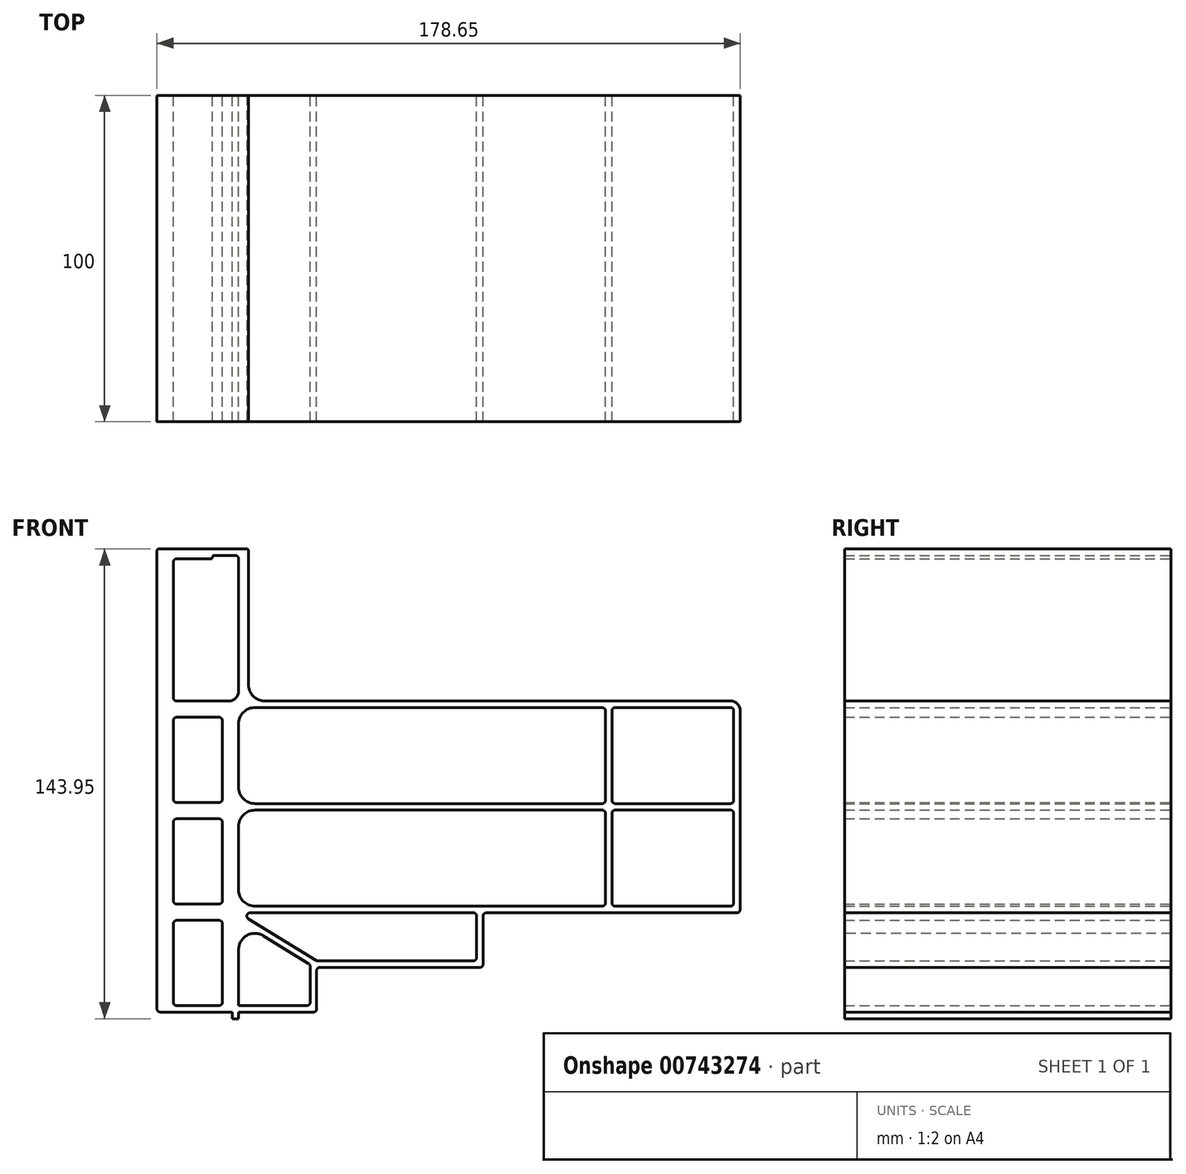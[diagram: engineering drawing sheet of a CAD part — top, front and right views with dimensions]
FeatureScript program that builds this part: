
annotation { "Feature Type Name" : "Feature", "Feature Type Description" : "" }
export const myFeature = defineFeature(function(context is Context, id is Id, definition is map)
    precondition{}
    {
        {
            var Q0;
            Q0=qCreatedBy(makeId("Front.planeOp"),FACE);
            var sketch = newSketch(context, id + "F0", { "sketchPlane" : qUnion([Q0])});
            skLineSegment(sketch, "E0", {"start": v(0, 0) * mm, "end": v(23, 0) * mm});
            skLineSegment(sketch, "E1", {"start": v(23, 0) * mm, "end": v(23, -2) * mm});
            skLineSegment(sketch, "E2", {"start": v(23, -2) * mm, "end": v(25, -2) * mm});
            skLineSegment(sketch, "E3", {"start": v(25, -2) * mm, "end": v(25, 0) * mm});
            skLineSegment(sketch, "E4", {"start": v(25, 0) * mm, "end": v(48.9, 0) * mm});
            skLineSegment(sketch, "E5", {"start": v(48.9, 0) * mm, "end": v(48.9, 13.72) * mm});
            skLineSegment(sketch, "E6", {"start": v(48.9, 15.72) * mm, "end": v(25, 30.47) * mm});
            skLineSegment(sketch, "E7", {"start": v(25, 30.47) * mm, "end": v(97.9, 30.47) * mm});
            skLineSegment(sketch, "E8", {"start": v(178.65, 30.47) * mm, "end": v(178.65, 95.36) * mm});
            skLineSegment(sketch, "E9", {"start": v(178.65, 95.36) * mm, "end": v(28, 95.36) * mm});
            skLineSegment(sketch, "E10", {"start": v(28, 141.95) * mm, "end": v(0, 141.95) * mm});
            skLineSegment(sketch, "E11", {"start": v(0, 141.95) * mm, "end": v(0, 0) * mm});
            skLineSegment(sketch, "E12", {"start": v(20, 90.36) * mm, "end": v(20, 64.24) * mm});
            skLineSegment(sketch, "E13", {"start": v(5, 33.12) * mm, "end": v(20, 33.12) * mm});
            skLineSegment(sketch, "E14", {"start": v(5, 33.12) * mm, "end": v(5, 59.24) * mm});
            skLineSegment(sketch, "E15", {"start": v(5, 59.24) * mm, "end": v(20, 59.24) * mm});
            skLineSegment(sketch, "E16", {"start": v(5, 64.24) * mm, "end": v(20, 64.24) * mm});
            skLineSegment(sketch, "E17.trimOffspring", {"start": v(5, 64.24) * mm, "end": v(5, 90.36) * mm});
            skLineSegment(sketch, "E18.trimOffspring", {"start": v(20, 59.24) * mm, "end": v(20, 33.12) * mm});
            skLineSegment(sketch, "E19", {"start": v(20, 28.12) * mm, "end": v(20, 2) * mm});
            skLineSegment(sketch, "E20", {"start": v(5, 2) * mm, "end": v(20, 2) * mm});
            skLineSegment(sketch, "E21", {"start": v(5, 2) * mm, "end": v(5, 28.12) * mm});
            skLineSegment(sketch, "E22", {"start": v(20, 28.12) * mm, "end": v(5, 28.12) * mm});
            skLineSegment(sketch, "E23", {"start": v(25, 28.12) * mm, "end": v(46.9, 14.6) * mm});
            skLineSegment(sketch, "E24", {"start": v(46.9, 14.6) * mm, "end": v(46.9, 2) * mm});
            skLineSegment(sketch, "E25", {"start": v(46.9, 2) * mm, "end": v(25, 2) * mm});
            skLineSegment(sketch, "E26", {"start": v(25, 2) * mm, "end": v(25, 28.12) * mm});
            skLineSegment(sketch, "E27", {"start": v(25, 32.47) * mm, "end": v(137.35, 32.47) * mm});
            skLineSegment(sketch, "E28", {"start": v(137.35, 32.47) * mm, "end": v(137.35, 61.92) * mm});
            skLineSegment(sketch, "E29", {"start": v(137.35, 61.92) * mm, "end": v(25, 61.92) * mm});
            skLineSegment(sketch, "E30", {"start": v(25, 61.92) * mm, "end": v(25, 32.47) * mm});
            skLineSegment(sketch, "E31", {"start": v(25, 93.36) * mm, "end": v(25, 63.92) * mm});
            skLineSegment(sketch, "E32", {"start": v(25, 63.92) * mm, "end": v(137.35, 63.92) * mm});
            skLineSegment(sketch, "E33", {"start": v(137.35, 63.92) * mm, "end": v(137.35, 93.36) * mm});
            skLineSegment(sketch, "E34", {"start": v(25, 93.36) * mm, "end": v(137.35, 93.36) * mm});
            skLineSegment(sketch, "E35", {"start": v(139.35, 93.36) * mm, "end": v(176.65, 93.36) * mm});
            skLineSegment(sketch, "E36", {"start": v(176.65, 93.36) * mm, "end": v(176.65, 63.92) * mm});
            skLineSegment(sketch, "E37", {"start": v(176.65, 63.92) * mm, "end": v(139.35, 63.92) * mm});
            skLineSegment(sketch, "E38", {"start": v(139.35, 63.92) * mm, "end": v(139.35, 93.36) * mm});
            skLineSegment(sketch, "E39", {"start": v(139.35, 61.92) * mm, "end": v(139.35, 32.47) * mm});
            skLineSegment(sketch, "E40", {"start": v(139.35, 32.47) * mm, "end": v(176.65, 32.47) * mm});
            skLineSegment(sketch, "E41", {"start": v(176.65, 32.47) * mm, "end": v(176.65, 61.92) * mm});
            skLineSegment(sketch, "E42", {"start": v(176.65, 61.92) * mm, "end": v(139.35, 61.92) * mm});
            skLineSegment(sketch, "E43", {"start": v(5, 33.12) * mm, "end": v(5, 28.12) * mm, "construction": true});
            skLineSegment(sketch, "E44", {"start": v(5, 64.24) * mm, "end": v(5, 59.24) * mm, "construction": true});
            skLineSegment(sketch, "E45", {"start": v(137.35, 93.36) * mm, "end": v(139.35, 93.36) * mm, "construction": true});
            skLineSegment(sketch, "E46", {"start": v(25, 63.92) * mm, "end": v(25, 61.92) * mm, "construction": true});
            skLineSegment(sketch, "E47", {"start": v(25, 32.47) * mm, "end": v(25, 30.47) * mm, "construction": true});
            skLineSegment(sketch, "E48", {"start": v(25, 28.12) * mm, "end": v(25, 30.47) * mm, "construction": true});
            skLineSegment(sketch, "E49", {"start": v(25, 2) * mm, "end": v(5, 2) * mm, "construction": true});
            skLineSegment(sketch, "E50", {"start": v(137.35, 32.47) * mm, "end": v(139.35, 32.47) * mm, "construction": true});
            skLineSegment(sketch, "E51", {"start": v(176.65, 61.92) * mm, "end": v(176.65, 63.92) * mm, "construction": true});
            skLineSegment(sketch, "E52", {"start": v(137.35, 63.92) * mm, "end": v(137.35, 61.92) * mm, "construction": true});
            skLineSegment(sketch, "E53", {"start": v(31.21, 24.29) * mm, "end": v(32.26, 25.99) * mm, "construction": true});
            skLineSegment(sketch, "E54", {"start": v(46.9, 8.3) * mm, "end": v(48.9, 8.3) * mm, "construction": true});
            skLineSegment(sketch, "E55", {"start": v(24.57, 2) * mm, "end": v(24.57, 0) * mm, "construction": true});
            skLineSegment(sketch, "E56", {"start": v(48.9, 15.72) * mm, "end": v(97.9, 15.72) * mm});
            skLineSegment(sketch, "E57", {"start": v(97.9, 15.72) * mm, "end": v(97.9, 30.47) * mm});
            skLineSegment(sketch, "E58", {"start": v(99.9, 30.47) * mm, "end": v(99.9, 13.72) * mm});
            skLineSegment(sketch, "E59", {"start": v(99.9, 13.72) * mm, "end": v(48.9, 13.72) * mm});
            skLineSegment(sketch, "E60.trimOffspring", {"start": v(99.9, 30.47) * mm, "end": v(178.65, 30.47) * mm});
            skLineSegment(sketch, "E61", {"start": v(139.35, 63.92) * mm, "end": v(137.35, 63.92) * mm, "construction": true});
            skLineSegment(sketch, "E62", {"start": v(137.35, 61.92) * mm, "end": v(139.35, 61.92) * mm, "construction": true});
            skLineSegment(sketch, "E63", {"start": v(97.9, 30.47) * mm, "end": v(99.9, 30.47) * mm, "construction": true});
            skLineSegment(sketch, "E64", {"start": v(5, 95.36) * mm, "end": v(5, 138.95) * mm});
            skLineSegment(sketch, "E65", {"start": v(5, 90.36) * mm, "end": v(20, 90.36) * mm});
            skLineSegment(sketch, "E66", {"start": v(74.4, 13.72) * mm, "end": v(74.4, 15.72) * mm, "construction": true});
            skLineSegment(sketch, "E67", {"start": v(25, 2) * mm, "end": v(25, 0) * mm, "construction": true});
            skLineSegment(sketch, "E68", {"start": v(25, 18) * mm, "end": v(20, 18) * mm, "construction": true});
            skLineSegment(sketch, "E69", {"start": v(5, 2) * mm, "end": v(0, 2) * mm, "construction": true});
            skLineSegment(sketch, "E70", {"start": v(176.65, 32.47) * mm, "end": v(176.65, 30.47) * mm, "construction": true});
            skLineSegment(sketch, "E71", {"start": v(176.65, 32.47) * mm, "end": v(178.65, 32.47) * mm, "construction": true});
            skLineSegment(sketch, "E72", {"start": v(5, 95.36) * mm, "end": v(25, 95.36) * mm});
            skLineSegment(sketch, "E73", {"start": v(28, 141.95) * mm, "end": v(28, 95.36) * mm});
            skLineSegment(sketch, "E74", {"start": v(25, 139.95) * mm, "end": v(25, 95.36) * mm});
            skLineSegment(sketch, "E75", {"start": v(5, 138.95) * mm, "end": v(17, 138.95) * mm});
            skLineSegment(sketch, "E76", {"start": v(17, 138.95) * mm, "end": v(17, 139.95) * mm});
            skLineSegment(sketch, "E77", {"start": v(17, 139.95) * mm, "end": v(25, 139.95) * mm});
            skSolve(sketch);
        }
        {
            var Q0;
            Q0=makeQuery(id+"F0.imprint","IMPRINT",FACE,{"disambiguationData":[TD([[makeQuery(id+"F0.imprint","IMPRINT",EDGE,{"derivedFrom":sQuery(id+"F0.wireOp",EDGE,"E0")}),1.0]])]});
            extrude(context, id + "F1", {"entities" : qUnion([Q0]), "depth" : 100 * mm, "offsetDistance" : 25 * mm});
        }
        {
            var Q0;
            Q0=makeQuery(id+"F1.opExtrude","SWEPT_EDGE",EDGE,{"disambiguationData":[OSD([sQuery(id+"F0.wireOp",EDGE,"E9"),sQuery(id+"F0.wireOp",EDGE,"E73")])]});
            var Q1;
            Q1=makeQuery(id+"F1.opExtrude","SWEPT_EDGE",EDGE,{"disambiguationData":[OSD([sQuery(id+"F0.wireOp",EDGE,"E23"),sQuery(id+"F0.wireOp",EDGE,"E26")])]});
            var Q2;
            Q2=makeQuery(id+"F1.opExtrude","SWEPT_EDGE",EDGE,{"disambiguationData":[OSD([sQuery(id+"F0.wireOp",EDGE,"E27"),sQuery(id+"F0.wireOp",EDGE,"E30")])]});
            var Q3;
            Q3=makeQuery(id+"F1.opExtrude","SWEPT_EDGE",EDGE,{"disambiguationData":[OSD([sQuery(id+"F0.wireOp",EDGE,"E29"),sQuery(id+"F0.wireOp",EDGE,"E30")])]});
            var Q4;
            Q4=makeQuery(id+"F1.opExtrude","SWEPT_EDGE",EDGE,{"disambiguationData":[OSD([sQuery(id+"F0.wireOp",EDGE,"E31"),sQuery(id+"F0.wireOp",EDGE,"E34")])]});
            var Q5;
            Q5=makeQuery(id+"F1.opExtrude","SWEPT_EDGE",EDGE,{"disambiguationData":[OSD([sQuery(id+"F0.wireOp",EDGE,"E31"),sQuery(id+"F0.wireOp",EDGE,"E32")])]});
            fillet(context, id + "F2", {"entities" : qUnion([Q0, Q1, Q2, Q3, Q4, Q5]), "radius" : 5 * mm, "tangentPropagation" : true, "allowEdgeOverflow" : false});
        }
        {
            var Q0;
            Q0=makeQuery(id+"F1.opExtrude","SWEPT_EDGE",EDGE,{"disambiguationData":[OSD([sQuery(id+"F0.wireOp",EDGE,"696LTCtU-8L7l-0TQZ-7p5k-baEngQwWw874"),sQuery(id+"F0.wireOp",EDGE,"E64")])]});
            var Q1;
            Q1=makeQuery(id+"F1.opExtrude","SWEPT_EDGE",EDGE,{"disambiguationData":[OSD([sQuery(id+"F0.wireOp",EDGE,"E16"),sQuery(id+"F0.wireOp",EDGE,"E17.trimOffspring")])]});
            var Q2;
            Q2=makeQuery(id+"F1.opExtrude","SWEPT_EDGE",EDGE,{"disambiguationData":[OSD([sQuery(id+"F0.wireOp",EDGE,"E13"),sQuery(id+"F0.wireOp",EDGE,"E14")])]});
            var Q3;
            Q3=makeQuery(id+"F1.opExtrude","SWEPT_EDGE",EDGE,{"disambiguationData":[OSD([sQuery(id+"F0.wireOp",EDGE,"E20"),sQuery(id+"F0.wireOp",EDGE,"E21")])]});
            var Q4;
            Q4=makeQuery(id+"F1.opExtrude","SWEPT_EDGE",EDGE,{"disambiguationData":[OSD([sQuery(id+"F0.wireOp",EDGE,"E64"),sQuery(id+"F0.wireOp",EDGE,"BG8pf7Ll-KLwd-1KIG-Txls-kzz8Mmku1XrW")])]});
            var Q5;
            Q5=makeQuery(id+"F1.opExtrude","SWEPT_EDGE",EDGE,{"disambiguationData":[OSD([sQuery(id+"F0.wireOp",EDGE,"E17.trimOffspring"),sQuery(id+"F0.wireOp",EDGE,"E65")])]});
            var Q6;
            Q6=makeQuery(id+"F1.opExtrude","SWEPT_EDGE",EDGE,{"disambiguationData":[OSD([sQuery(id+"F0.wireOp",EDGE,"E14"),sQuery(id+"F0.wireOp",EDGE,"E15")])]});
            var Q7;
            Q7=makeQuery(id+"F1.opExtrude","SWEPT_EDGE",EDGE,{"disambiguationData":[OSD([sQuery(id+"F0.wireOp",EDGE,"E21"),sQuery(id+"F0.wireOp",EDGE,"E22")])]});
            var Q8;
            Q8=makeQuery(id+"F1.opExtrude","SWEPT_EDGE",EDGE,{"disambiguationData":[OSD([sQuery(id+"F0.wireOp",EDGE,"E19"),sQuery(id+"F0.wireOp",EDGE,"E22")])]});
            var Q9;
            Q9=makeQuery(id+"F1.opExtrude","SWEPT_EDGE",EDGE,{"disambiguationData":[OSD([sQuery(id+"F0.wireOp",EDGE,"E15"),sQuery(id+"F0.wireOp",EDGE,"E18.trimOffspring")])]});
            var Q10;
            Q10=makeQuery(id+"F1.opExtrude","SWEPT_EDGE",EDGE,{"disambiguationData":[OSD([sQuery(id+"F0.wireOp",EDGE,"E12"),sQuery(id+"F0.wireOp",EDGE,"E65")])]});
            var Q11;
            Q11=makeQuery(id+"F1.opExtrude","SWEPT_EDGE",EDGE,{"disambiguationData":[OSD([sQuery(id+"F0.wireOp",EDGE,"JW9Dk7mF-qHn0-8jiC-juDo-dlRvJ3E6QT4r"),sQuery(id+"F0.wireOp",EDGE,"BG8pf7Ll-KLwd-1KIG-Txls-kzz8Mmku1XrW")])]});
            var Q12;
            Q12=makeQuery(id+"F1.opExtrude","SWEPT_EDGE",EDGE,{"disambiguationData":[OSD([sQuery(id+"F0.wireOp",EDGE,"JW9Dk7mF-qHn0-8jiC-juDo-dlRvJ3E6QT4r"),sQuery(id+"F0.wireOp",EDGE,"696LTCtU-8L7l-0TQZ-7p5k-baEngQwWw874")])]});
            var Q13;
            Q13=makeQuery(id+"F1.opExtrude","SWEPT_EDGE",EDGE,{"disambiguationData":[OSD([sQuery(id+"F0.wireOp",EDGE,"E12"),sQuery(id+"F0.wireOp",EDGE,"E16")])]});
            var Q14;
            Q14=makeQuery(id+"F1.opExtrude","SWEPT_EDGE",EDGE,{"disambiguationData":[OSD([sQuery(id+"F0.wireOp",EDGE,"E13"),sQuery(id+"F0.wireOp",EDGE,"E18.trimOffspring")])]});
            var Q15;
            Q15=makeQuery(id+"F1.opExtrude","SWEPT_EDGE",EDGE,{"disambiguationData":[OSD([sQuery(id+"F0.wireOp",EDGE,"E19"),sQuery(id+"F0.wireOp",EDGE,"E20")])]});
            var Q16;
            Q16=makeQuery(id+"F1.opExtrude","SWEPT_EDGE",EDGE,{"disambiguationData":[OSD([sQuery(id+"F0.wireOp",EDGE,"E24"),sQuery(id+"F0.wireOp",EDGE,"E25")])]});
            var Q17;
            Q17=makeQuery(id+"F1.opExtrude","SWEPT_EDGE",EDGE,{"disambiguationData":[OSD([sQuery(id+"F0.wireOp",EDGE,"E23"),sQuery(id+"F0.wireOp",EDGE,"E24")])]});
            var Q18;
            Q18=makeQuery(id+"F1.opExtrude","SWEPT_EDGE",EDGE,{"disambiguationData":[OSD([sQuery(id+"F0.wireOp",EDGE,"E6"),sQuery(id+"F0.wireOp",EDGE,"E7")])]});
            var Q19;
            Q19=makeQuery(id+"F1.opExtrude","SWEPT_EDGE",EDGE,{"disambiguationData":[OSD([sQuery(id+"F0.wireOp",EDGE,"E56"),sQuery(id+"F0.wireOp",EDGE,"E57")])]});
            var Q20;
            Q20=makeQuery(id+"F1.opExtrude","SWEPT_EDGE",EDGE,{"disambiguationData":[OSD([sQuery(id+"F0.wireOp",EDGE,"E7"),sQuery(id+"F0.wireOp",EDGE,"E57")])]});
            var Q21;
            Q21=makeQuery(id+"F1.opExtrude","SWEPT_EDGE",EDGE,{"disambiguationData":[OSD([sQuery(id+"F0.wireOp",EDGE,"E28"),sQuery(id+"F0.wireOp",EDGE,"E29")])]});
            var Q22;
            Q22=makeQuery(id+"F1.opExtrude","SWEPT_EDGE",EDGE,{"disambiguationData":[OSD([sQuery(id+"F0.wireOp",EDGE,"E33"),sQuery(id+"F0.wireOp",EDGE,"E34")])]});
            var Q23;
            Q23=makeQuery(id+"F1.opExtrude","SWEPT_EDGE",EDGE,{"disambiguationData":[OSD([sQuery(id+"F0.wireOp",EDGE,"E32"),sQuery(id+"F0.wireOp",EDGE,"E33")])]});
            var Q24;
            Q24=makeQuery(id+"F1.opExtrude","SWEPT_EDGE",EDGE,{"disambiguationData":[OSD([sQuery(id+"F0.wireOp",EDGE,"E27"),sQuery(id+"F0.wireOp",EDGE,"E28")])]});
            var Q25;
            Q25=makeQuery(id+"F1.opExtrude","SWEPT_EDGE",EDGE,{"disambiguationData":[OSD([sQuery(id+"F0.wireOp",EDGE,"E40"),sQuery(id+"F0.wireOp",EDGE,"E41")])]});
            var Q26;
            Q26=makeQuery(id+"F1.opExtrude","SWEPT_EDGE",EDGE,{"disambiguationData":[OSD([sQuery(id+"F0.wireOp",EDGE,"E36"),sQuery(id+"F0.wireOp",EDGE,"E37")])]});
            var Q27;
            Q27=makeQuery(id+"F1.opExtrude","SWEPT_EDGE",EDGE,{"disambiguationData":[OSD([sQuery(id+"F0.wireOp",EDGE,"E37"),sQuery(id+"F0.wireOp",EDGE,"E38")])]});
            var Q28;
            Q28=makeQuery(id+"F1.opExtrude","SWEPT_EDGE",EDGE,{"disambiguationData":[OSD([sQuery(id+"F0.wireOp",EDGE,"E39"),sQuery(id+"F0.wireOp",EDGE,"E42")])]});
            var Q29;
            Q29=makeQuery(id+"F1.opExtrude","SWEPT_EDGE",EDGE,{"disambiguationData":[OSD([sQuery(id+"F0.wireOp",EDGE,"E35"),sQuery(id+"F0.wireOp",EDGE,"E38")])]});
            var Q30;
            Q30=makeQuery(id+"F1.opExtrude","SWEPT_EDGE",EDGE,{"disambiguationData":[OSD([sQuery(id+"F0.wireOp",EDGE,"E35"),sQuery(id+"F0.wireOp",EDGE,"E36")])]});
            var Q31;
            Q31=makeQuery(id+"F1.opExtrude","SWEPT_EDGE",EDGE,{"disambiguationData":[OSD([sQuery(id+"F0.wireOp",EDGE,"E41"),sQuery(id+"F0.wireOp",EDGE,"E42")])]});
            var Q32;
            Q32=makeQuery(id+"F1.opExtrude","SWEPT_EDGE",EDGE,{"disambiguationData":[OSD([sQuery(id+"F0.wireOp",EDGE,"E39"),sQuery(id+"F0.wireOp",EDGE,"E40")])]});
            var Q33;
            Q33=makeQuery(id+"F1.opExtrude","SWEPT_EDGE",EDGE,{"disambiguationData":[OSD([sQuery(id+"F0.wireOp",EDGE,"E58"),sQuery(id+"F0.wireOp",EDGE,"E60.trimOffspring")])]});
            var Q34;
            Q34=makeQuery(id+"F1.opExtrude","SWEPT_EDGE",EDGE,{"disambiguationData":[OSD([sQuery(id+"F0.wireOp",EDGE,"E5"),sQuery(id+"F0.wireOp",EDGE,"E59")])]});
            var Q35;
            Q35=makeQuery(id+"F1.opExtrude","SWEPT_EDGE",EDGE,{"disambiguationData":[OSD([sQuery(id+"F0.wireOp",EDGE,"E4"),sQuery(id+"F0.wireOp",EDGE,"E5")])]});
            var Q36;
            Q36=makeQuery(id+"F1.opExtrude","SWEPT_EDGE",EDGE,{"disambiguationData":[OSD([sQuery(id+"F0.wireOp",EDGE,"E0"),sQuery(id+"F0.wireOp",EDGE,"E11")])]});
            var Q37;
            Q37=makeQuery(id+"F1.opExtrude","SWEPT_EDGE",EDGE,{"disambiguationData":[OSD([sQuery(id+"F0.wireOp",EDGE,"E6"),sQuery(id+"F0.wireOp",EDGE,"E56")])]});
            var Q38;
            Q38=makeQuery(id+"F1.opExtrude","SWEPT_EDGE",EDGE,{"disambiguationData":[OSD([sQuery(id+"F0.wireOp",EDGE,"E58"),sQuery(id+"F0.wireOp",EDGE,"E59")])]});
            var Q39;
            Q39=makeQuery(id+"F1.opExtrude","SWEPT_EDGE",EDGE,{"disambiguationData":[OSD([sQuery(id+"F0.wireOp",EDGE,"E8"),sQuery(id+"F0.wireOp",EDGE,"E60.trimOffspring")])]});
            var Q40;
            Q40=makeQuery(id+"F1.opExtrude","SWEPT_EDGE",EDGE,{"disambiguationData":[OSD([sQuery(id+"F0.wireOp",EDGE,"E74"),sQuery(id+"F0.wireOp",EDGE,"E77")])]});
            fillet(context, id + "F3", {"entities" : qUnion([Q0, Q1, Q2, Q3, Q4, Q5, Q6, Q7, Q8, Q9, Q10, Q11, Q12, Q13, Q14, Q15, Q16, Q17, Q18, Q19, Q20, Q21, Q22, Q23, Q24, Q25, Q26, Q27, Q28, Q29, Q30, Q31, Q32, Q33, Q34, Q35, Q36, Q37, Q38, Q39, Q40]), "radius" : 1 * mm, "tangentPropagation" : true, "allowEdgeOverflow" : false});
        }
        {
            var Q0;
            Q0=makeQuery(id+"F1.opExtrude","SWEPT_EDGE",EDGE,{"disambiguationData":[OSD([sQuery(id+"F0.wireOp",EDGE,"UcFooWco-jjp3-GLu6-jal5-oRo9MLq9WRDR"),sQuery(id+"F0.wireOp",EDGE,"E10")])]});
            var Q1;
            Q1=makeQuery(id+"F1.opExtrude","SWEPT_EDGE",EDGE,{"disambiguationData":[OSD([sQuery(id+"F0.wireOp",EDGE,"E10"),sQuery(id+"F0.wireOp",EDGE,"E11")])]});
            fillet(context, id + "F4", {"entities" : qUnion([Q0, Q1]), "radius" : 0.5 * mm, "tangentPropagation" : true, "allowEdgeOverflow" : false});
        }
        {
            var Q0;
            Q0=makeQuery(id+"F1.opExtrude","SWEPT_EDGE",EDGE,{"disambiguationData":[OSD([sQuery(id+"F0.wireOp",EDGE,"E8"),sQuery(id+"F0.wireOp",EDGE,"E9")])]});
            var Q1;
            Q1=makeQuery(id+"F1.opExtrude","SWEPT_EDGE",EDGE,{"disambiguationData":[OSD([sQuery(id+"F0.wireOp",EDGE,"E58"),sQuery(id+"F0.wireOp",EDGE,"E59")])]});
            var Q2;
            Q2=makeQuery(id+"F1.opExtrude","SWEPT_EDGE",EDGE,{"disambiguationData":[OSD([sQuery(id+"F0.wireOp",EDGE,"E8"),sQuery(id+"F0.wireOp",EDGE,"E60.trimOffspring")])]});
            var Q3;
            Q3=makeQuery(id+"F1.opExtrude","SWEPT_EDGE",EDGE,{"disambiguationData":[OSD([sQuery(id+"F0.wireOp",EDGE,"E58"),sQuery(id+"F0.wireOp",EDGE,"E60.trimOffspring")])]});
            fillet(context, id + "F5", {"entities" : qUnion([Q0, Q1, Q2, Q3]), "radius" : 3 * mm, "tangentPropagation" : true, "allowEdgeOverflow" : false});
        }
        {
            var Q0;
            Q0=makeQuery(id+"F1.opExtrude","SWEPT_EDGE",EDGE,{"disambiguationData":[OSD([sQuery(id+"F0.wireOp",EDGE,"E76"),sQuery(id+"F0.wireOp",EDGE,"E77")])]});
            var Q1;
            Q1=makeQuery(id+"F1.opExtrude","SWEPT_EDGE",EDGE,{"disambiguationData":[OSD([sQuery(id+"F0.wireOp",EDGE,"E75"),sQuery(id+"F0.wireOp",EDGE,"E76")])]});
            fillet(context, id + "F6", {"entities" : qUnion([Q0, Q1]), "radius" : 0.5 * mm, "tangentPropagation" : true, "allowEdgeOverflow" : false});
        }
        {
            var Q0;
            Q0=makeQuery(id+"F1.opExtrude","SWEPT_EDGE",EDGE,{"disambiguationData":[OSD([sQuery(id+"F0.wireOp",EDGE,"E72"),sQuery(id+"F0.wireOp",EDGE,"E74")])]});
            fillet(context, id + "F7", {"entities" : qUnion([Q0]), "radius" : 3 * mm, "tangentPropagation" : true, "allowEdgeOverflow" : false});
        }
    });
